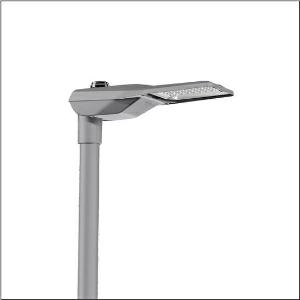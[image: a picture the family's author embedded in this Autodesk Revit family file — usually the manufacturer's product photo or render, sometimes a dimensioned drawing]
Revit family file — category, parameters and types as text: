
# Revit family: streetlight_sl_21_mini___p1_0a_5xe6a37n08hb_d726
name_source: partatom
category: Lighting Fixtures
units: mm (PartAtom-declared; Revit-internal decimal feet)

## family parameters
Cut with Voids When Loaded = No
Host = Face
Light Source = No
Part Type = Normal
Room Calculation Point = No
Round Connector Dimension = Use Diameter
Shared = No

## types (1)
- --- (1 x LED, 9040 lm, 66 W, 3000K)
    Apparent Load = 66 VA
    CIE Flux Codes = 21 50 90 100 100
    Color Rendering = 70
    Color Temperature = 3000K
    Default Elevation = 1800 mm
    Description = Streetlight SL 21 mini, mast luminaire, primary light control with lens, of PMMA, primary optical cover: cover, of toughened safety glass, transparent, light distribution: P1.0a, light emission: direct distribution, primary light characteristic: asymmetric, installation type: side-entry, LED, 3G 1.5mm², High Power LED, rated luminous flux: 9.040lm, luminous efficacy: 137lm/W, light colour: 730, colour temperature: 3000K, control gear: NEMA (7pin), control: overheat protection, pre-setting: linear dimming characteristic, constant luminous flux control, time-dependent luminous flux control, flexible luminous flux parameterisation, mains connection: 230..240V, AC, 50/60Hz, connection cable pre-assembled, cable length: 8,5m, wiring characteristics: H07RN-F, start of lifetime: 66W, end of service life: 69W, reduction: 30W, luminaire housing, of diecast aluminium (EN AC-44300), powder-coated, Siteco® metallic grey (DB 702S), corrosivity category C5 mid according to DIN EN ISO 12944, multi-level sealing system, sealing non-destructively replaceable, inclination adjustable: 0°, 5°, 10°, 15°, length: 628mm, width: 235mm, height: 110mm, spigot size: 42mm (side-entry), mounting height: 4..8m, protection rating (complete): IP66, insulation class (complete): insulation class I (protective earthing), certification: CE, ENEC, ENEC+, VDE, impact resistance: IK09, permissible operating ambient temperature for outdoor applications: -40..+50°C, standard-compliant lighting for roads and squares, packaging unit: 1 piece

Light Distribution: P1.0a
    Height = 110 mm
    Lamp = 1 x LED
    Lamp Light Flux = 9040 lm
    Lamp Power = 66 W
    Lamp count = 1
    Length = 625 mm
    Luminous efficacy = 137 lm/W
    Manufacturer = Siteco
    ModVariant = No
    Model = 5XE6A37N08HB
    Number of Poles = 1
    OnlyDefault = Yes
    Power Factor = 1
    Product Name = Streetlight SL 21 mini | P1.0a
    Product group = mast luminaire | pylon top
    ProductGroupID = 6100
    Protection Class = Protection class I
    Protection Degree = IP 66
    RLX_Detail_Level = 1
    RLX_Emergency_Light_Flux = 0 lm
    RLX_Emergency_Type = 0
    RLX_Emergency_Type_DB = No
    RlxData = <blob elided: 103497 chars, md5=73951263>
    Socket = socket
    Standby Power = 0 W
    System Light Flux = 9040 lm
    System Power = 66 W
    Type Comments = factory setting: luminous flux: 100 % | dim-lin: 254 | 670 mA
    Type Image = l_1294379.jpg
    URL = http://relux.com
    VarID = @adj_129984
    Voltage = 0 V
    Weight = 0.00 kg
    Width = 234 mm

## geometry (parser evidence)
native form markers: Blend x4, Sweep x9
no freeform markers — native parametric forms only
